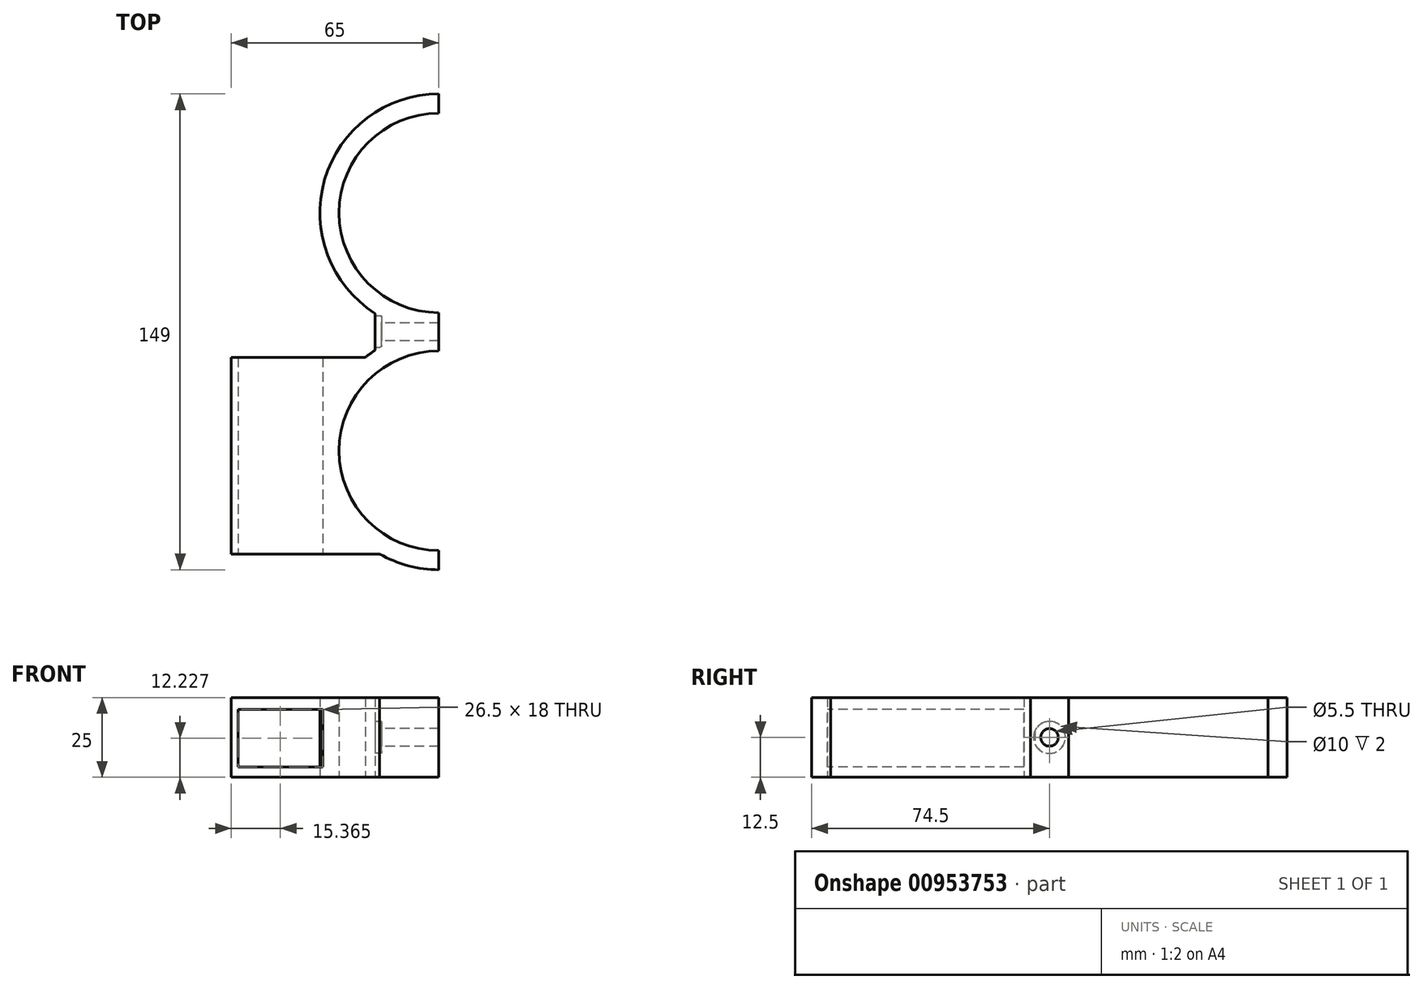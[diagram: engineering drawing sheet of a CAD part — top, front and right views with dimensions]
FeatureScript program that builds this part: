
annotation { "Feature Type Name" : "Feature", "Feature Type Description" : "" }
export const myFeature = defineFeature(function(context is Context, id is Id, definition is map)
    precondition{}
    {
        {
            var Q0;
            Q0=qCreatedBy(makeId("Top.planeOp"),FACE);
            var sketch = newSketch(context, id + "F0", { "sketchPlane" : qUnion([Q0])});
            skCircle(sketch, "E0", {"center": v(0, 37.25) * mm, "radius": 37.25 * mm});
            skCircle(sketch, "E1", {"center": v(0, 37.25) * mm, "radius": 31.25 * mm});
            skCircle(sketch, "E2", {"center": v(0, -37.25) * mm, "radius": 37.25 * mm});
            skCircle(sketch, "E3", {"center": v(0, -37.25) * mm, "radius": 31.25 * mm});
            skLineSegment(sketch, "E4.bottom", {"start": v(0, 74.5) * mm, "end": v(0, 74.5) * mm});
            skLineSegment(sketch, "E4.top", {"start": v(0, -74.5) * mm, "end": v(0, -74.5) * mm});
            skLineSegment(sketch, "E4.left", {"start": v(0, 74.5) * mm, "end": v(0, -74.5) * mm});
            skLineSegment(sketch, "E4.right", {"start": v(0, 74.5) * mm, "end": v(0, -74.5) * mm});
            skLineSegment(sketch, "E5", {"start": v(-19.91, 5.77) * mm, "end": v(-19.91, -5.77) * mm});
            skLineSegment(sketch, "E6", {"start": v(19.91, 5.77) * mm, "end": v(19.91, -5.77) * mm});
            skPoint(sketch, "E7.middle", {"position": v(-31.25, -37.25) * mm});
            skLineSegment(sketch, "E8.bottom", {"start": v(-31.25, -12.78) * mm, "end": v(-48.75, -12.78) * mm});
            skLineSegment(sketch, "E8.top", {"start": v(-31.25, -64.78) * mm, "end": v(-48.75, -64.78) * mm});
            skLineSegment(sketch, "E8.left", {"start": v(-31.25, -12.78) * mm, "end": v(-31.25, -16.98) * mm});
            skLineSegment(sketch, "E8.right", {"start": v(-48.75, -12.78) * mm, "end": v(-48.75, -64.78) * mm});
            skPoint(sketch, "E8.middle", {"position": v(-40, -38.78) * mm});
            skLineSegment(sketch, "E9.bottom", {"start": v(-65, -8) * mm, "end": v(-15, -8) * mm});
            skLineSegment(sketch, "E9.top", {"start": v(-65, -69.56) * mm, "end": v(-15, -69.56) * mm});
            skLineSegment(sketch, "E9.left", {"start": v(-65, -8) * mm, "end": v(-65, -69.56) * mm});
            skLineSegment(sketch, "E9.right", {"start": v(-15, -3.15) * mm, "end": v(-15, -8) * mm});
            skLineSegment(sketch, "E10.trimOffspring", {"start": v(-15, -69.56) * mm, "end": v(-15, -71.35) * mm});
            skLineSegment(sketch, "E11.trimOffspring", {"start": v(-31.25, -57.52) * mm, "end": v(-31.25, -64.78) * mm});
            skSolve(sketch);
        }
        {
            var Q0;
            {var subQ0=sQuery(id+"F0.wireOp",EDGE,"E4.right");var subQ4=sQuery(id+"F0.wireOp",EDGE,"E1");var subQ6=makeQuery(id+"F0.imprint","INTERSECT",VERTEX,{"disambiguationData":[OD(0.0)],"derivedFrom":[subQ4,subQ0]});Q0=makeQuery(id+"F0.imprint","IMPRINT",FACE,{"disambiguationData":[TD([[makeQuery(id+"F0.imprint","IMPRINT",EDGE,{"disambiguationData":[TD([[subQ6,-1.0]])],"derivedFrom":subQ4}),-1.0]])]});}
            var Q1;
            {var subQ0=sQuery(id+"F0.wireOp",EDGE,"E4.right");var subQ4=sQuery(id+"F0.wireOp",EDGE,"E3");var subQ5=makeQuery(id+"F0.imprint","INTERSECT",VERTEX,{"disambiguationData":[OD(0.0)],"derivedFrom":[subQ4,subQ0]});Q1=makeQuery(id+"F0.imprint","IMPRINT",FACE,{"disambiguationData":[TD([[makeQuery(id+"F0.imprint","IMPRINT",EDGE,{"disambiguationData":[TD([[subQ5,-1.0]])],"derivedFrom":subQ4}),-1.0]])]});}
            var Q2;
            {var subQ0=sQuery(id+"F0.wireOp",EDGE,"E5");Q2=makeQuery(id+"F0.imprint","IMPRINT",FACE,{"disambiguationData":[TD([[makeQuery(id+"F0.imprint","IMPRINT",EDGE,{"derivedFrom":subQ0}),1.0]])]});}
            var Q3;
            {var subQ0=sQuery(id+"F0.wireOp",EDGE,"E8.left");var subQ1=sQuery(id+"F0.wireOp",EDGE,"E2");var subQ2=makeQuery(id+"F0.imprint","INTERSECT",VERTEX,{"disambiguationData":[OD(0.0)],"derivedFrom":[subQ1,subQ0]});Q3=makeQuery(id+"F0.imprint","IMPRINT",FACE,{"disambiguationData":[TD([[makeQuery(id+"F0.imprint","IMPRINT",EDGE,{"disambiguationData":[TD([[subQ2,-1.0]])],"derivedFrom":subQ1}),1.0]])]});}
            var Q4;
            {var subQ5=sQuery(id+"F0.wireOp",EDGE,"E2");var subQ7=makeQuery(id+"F0.imprint","INTERSECT",VERTEX,{"derivedFrom":[subQ5,sQuery(id+"F0.wireOp",EDGE,"E10.trimOffspring")]});Q4=makeQuery(id+"F0.imprint","IMPRINT",FACE,{"disambiguationData":[TD([[makeQuery(id+"F0.imprint","IMPRINT",EDGE,{"disambiguationData":[TD([[subQ7,1.0]])],"derivedFrom":subQ5}),1.0]])]});}
            extrude(context, id + "F1", {"entities" : qUnion([Q0, Q1, Q2, Q3, Q4]), "depth" : 25 * mm, "offsetDistance" : 25 * mm});
        }
        {
            var Q0;
            Q0=makeQuery(id+"F1.opExtrude","SWEPT_FACE",FACE,{"disambiguationData":[OSD([sQuery(id+"F0.wireOp",EDGE,"E5")])]});
            var sketch = newSketch(context, id + "F2", { "sketchPlane" : qUnion([Q0])});
            skCircle(sketch, "E12", {"center": v(0, 12.5) * mm, "radius": 2.75 * mm});
            skPoint(sketch, "E12.centerSnap0", {"position": v(5.77, 12.5) * mm});
            skSolve(sketch);
        }
        {
            var Q0;
            Q0 = qSketchRegion(id + "F2", true);
            extrude(context, id + "F3", {"entities" : qUnion([Q0]), "operationType" : NewBodyOperationType.REMOVE, "endBound" : BoundingType.THROUGH_ALL, "oppositeDirection" : true, "depth" : 25 * mm, "offsetDistance" : 25 * mm});
        }
        {
            var Q0;
            Q0=makeQuery(id+"F1.opExtrude","SWEPT_FACE",FACE,{"disambiguationData":[OSD([sQuery(id+"F0.wireOp",EDGE,"E5")])]});
            var sketch = newSketch(context, id + "F4", { "sketchPlane" : qUnion([Q0])});
            skCircle(sketch, "E13", {"center": v(0, 12.5) * mm, "radius": 5 * mm});
            skSolve(sketch);
        }
        {
            var Q0;
            Q0 = qSketchRegion(id + "F4", true);
            extrude(context, id + "F5", {"entities" : qUnion([Q0]), "operationType" : NewBodyOperationType.REMOVE, "oppositeDirection" : true, "depth" : 2 * mm, "offsetDistance" : 25 * mm});
        }
        {
            var Q0;
            {var subQ1=sQuery(id+"F0.wireOp",EDGE,"E8.bottom");Q0=makeQuery(id+"F0.imprint","IMPRINT",FACE,{"disambiguationData":[TD([[makeQuery(id+"F0.imprint","IMPRINT",EDGE,{"derivedFrom":subQ1}),1.0]])]});}
            var Q1;
            {var subQ7=sQuery(id+"F0.wireOp",EDGE,"E8.bottom");Q1=makeQuery(id+"F0.imprint","IMPRINT",FACE,{"disambiguationData":[TD([[makeQuery(id+"F0.imprint","IMPRINT",EDGE,{"derivedFrom":subQ7}),-1.0]])]});}
            var Q2;
            {var subQ2=sQuery(id+"F0.wireOp",EDGE,"E9.right");Q2=makeQuery(id+"F0.imprint","IMPRINT",FACE,{"disambiguationData":[TD([[makeQuery(id+"F0.imprint","IMPRINT",EDGE,{"derivedFrom":subQ2}),-1.0]])]});}
            extrude(context, id + "F6", {"entities" : qUnion([Q0, Q1, Q2]), "operationType" : NewBodyOperationType.ADD, "depth" : 25 * mm, "offsetDistance" : 25 * mm});
        }
        {
            var Q0;
            Q0=makeQuery(id+"F6.opExtrude","SWEPT_FACE",FACE,{"disambiguationData":[OSD([sQuery(id+"F0.wireOp",EDGE,"E9.top")])]});
            var sketch = newSketch(context, id + "F7", { "sketchPlane" : qUnion([Q0])});
            skLineSegment(sketch, "E14.bottom", {"start": v(-36.39, 3.23) * mm, "end": v(-62.89, 3.23) * mm});
            skLineSegment(sketch, "E14.top", {"start": v(-36.39, 21.23) * mm, "end": v(-62.89, 21.23) * mm});
            skLineSegment(sketch, "E14.left", {"start": v(-36.39, 3.23) * mm, "end": v(-36.39, 21.23) * mm});
            skLineSegment(sketch, "E14.right", {"start": v(-62.89, 3.23) * mm, "end": v(-62.89, 21.23) * mm});
            skPoint(sketch, "E14.middle", {"position": v(-49.64, 12.23) * mm});
            skSolve(sketch);
        }
        {
            var Q0;
            Q0=makeQuery(id+"F7.imprint","IMPRINT",FACE,{"disambiguationData":[TD([[makeQuery(id+"F7.imprint","IMPRINT",EDGE,{"derivedFrom":sQuery(id+"F7.wireOp",EDGE,"E14.bottom")}),-1.0]])]});
            extrude(context, id + "F8", {"entities" : qUnion([Q0]), "operationType" : NewBodyOperationType.REMOVE, "endBound" : BoundingType.UP_TO_NEXT, "oppositeDirection" : true, "depth" : 25 * mm, "offsetDistance" : 25 * mm});
        }
    });
